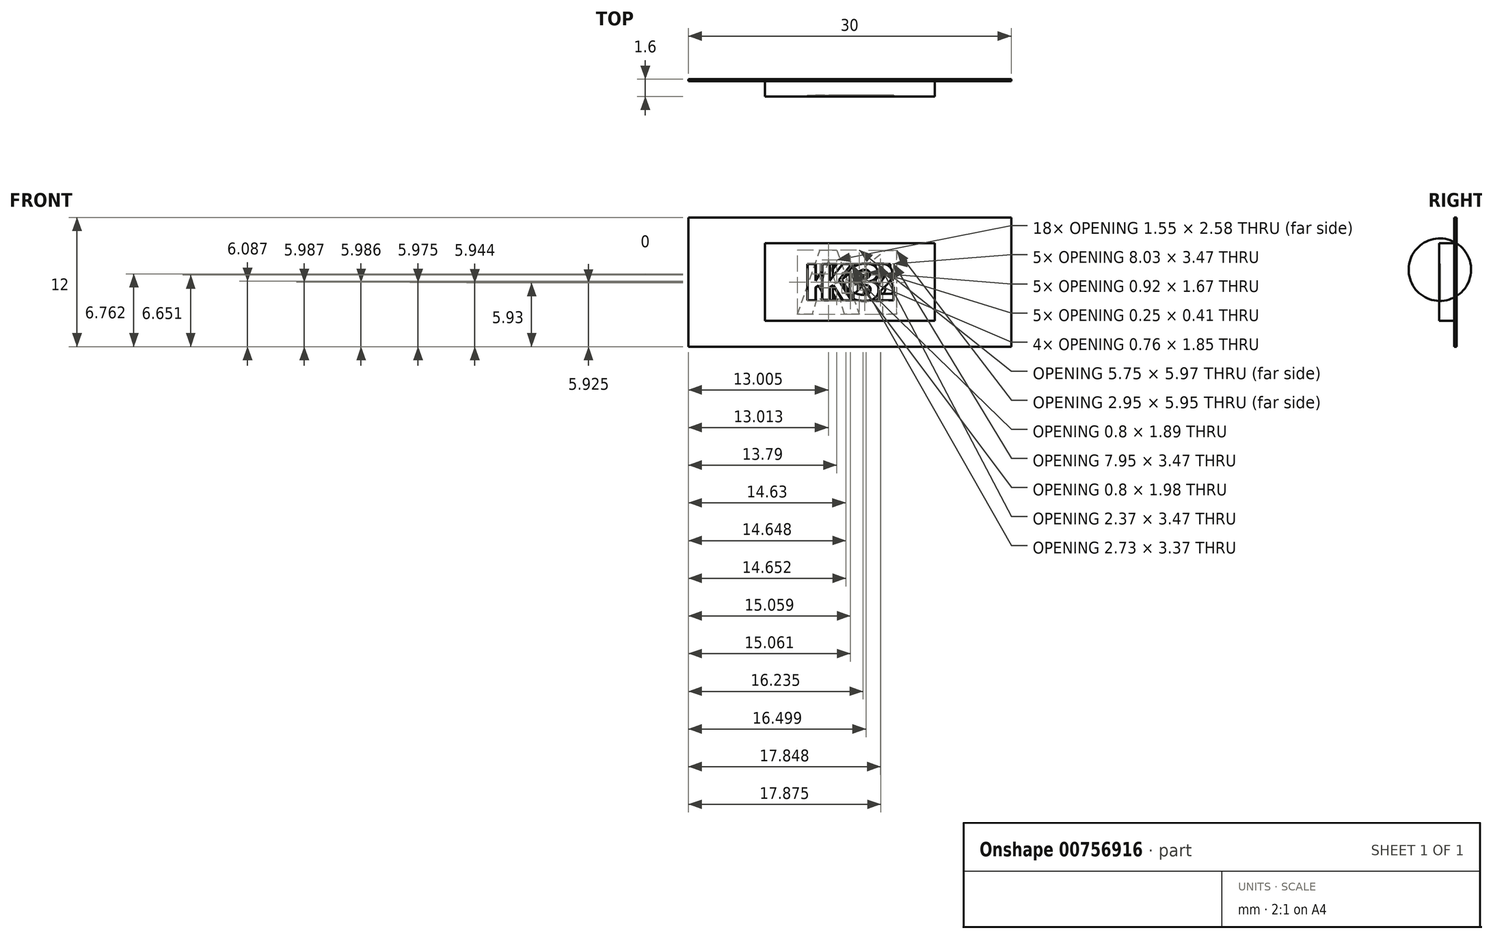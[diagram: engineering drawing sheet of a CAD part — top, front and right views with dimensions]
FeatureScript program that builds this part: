
annotation { "Feature Type Name" : "Feature", "Feature Type Description" : "" }
export const myFeature = defineFeature(function(context is Context, id is Id, definition is map)
    precondition{}
    {
        {
            var Q0;
            Q0=qCreatedBy(makeId("Front.planeOp"),FACE);
            var sketch = newSketch(context, id + "F0", { "sketchPlane" : qUnion([Q0])});
            skLineSegment(sketch, "E0.bottom", {"start": v(15, -6) * mm, "end": v(-15, -6) * mm});
            skLineSegment(sketch, "E0.top", {"start": v(15, 6) * mm, "end": v(-15, 6) * mm});
            skLineSegment(sketch, "E0.left", {"start": v(15, -6) * mm, "end": v(15, 6) * mm});
            skLineSegment(sketch, "E0.right", {"start": v(-15, -6) * mm, "end": v(-15, 6) * mm});
            skPoint(sketch, "E0.middle", {"position": v(0, 0) * mm});
            skSolve(sketch);
        }
        {
            var Q0;
            Q0 = qSketchRegion(id + "F0", true);
            extrude(context, id + "F1", {"entities" : qUnion([Q0]), "depth" : 0.2 * mm, "offsetDistance" : 25 * mm});
        }
        {
            var Q0;
            Q0=makeQuery(id+"F1.opExtrude","CAP_FACE",FACE,{"disambiguationData":[OSD([sQuery(id+"F0.wireOp",EDGE,"E0.bottom"),sQuery(id+"F0.wireOp",EDGE,"E0.top"),sQuery(id+"F0.wireOp",EDGE,"E0.left"),sQuery(id+"F0.wireOp",EDGE,"E0.right")])],"isStart":false});
            var sketch = newSketch(context, id + "F2", { "sketchPlane" : qUnion([Q0])});
            skLineSegment(sketch, "E1.bottom", {"start": v(4.87, -3) * mm, "end": v(-4.87, -3) * mm, "construction": true});
            skLineSegment(sketch, "E1.top", {"start": v(4.87, 3) * mm, "end": v(-4.87, 3) * mm, "construction": true});
            skLineSegment(sketch, "E1.left", {"start": v(4.87, -3) * mm, "end": v(4.87, 3) * mm, "construction": true});
            skLineSegment(sketch, "E1.right", {"start": v(-4.87, -3) * mm, "end": v(-4.87, 3) * mm, "construction": true});
            skPoint(sketch, "E1.middle", {"position": v(0, 0) * mm});
            skText(sketch, "E2", { "text": "A1", "fontName": "OpenSans-Bold.ttf"});
            const initialGuessF2  = {"E2": [-0.00487, -0.003, 1, 0, 0.006]};
            skSetInitialGuess(sketch, initialGuessF2);
            skSolve(sketch);
        }
        {
            var Q0;
            Q0 = qSketchRegion(id + "F2", true);
            extrude(context, id + "F3", {"entities" : qUnion([Q0]), "operationType" : NewBodyOperationType.REMOVE, "oppositeDirection" : true, "depth" : 0.1 * mm, "offsetDistance" : 25 * mm});
        }
        {
            var Q0;
            Q0=makeQuery(id+"F3.boolean.opBoolean","COPY",FACE,{"derivedFrom":makeQuery(id+"F3.opExtrude","CAP_FACE",FACE,{"disambiguationData":[OSD([sQuery(id+"F2.wireOp",EDGE,"E2.sketch_text.stroke-0"),sQuery(id+"F2.wireOp",EDGE,"E2.sketch_text.stroke-1"),sQuery(id+"F2.wireOp",EDGE,"E2.sketch_text.stroke-2"),sQuery(id+"F2.wireOp",EDGE,"E2.sketch_text.stroke-3"),sQuery(id+"F2.wireOp",EDGE,"E2.sketch_text.stroke-4"),sQuery(id+"F2.wireOp",EDGE,"E2.sketch_text.stroke-5"),sQuery(id+"F2.wireOp",EDGE,"E2.sketch_text.stroke-6"),sQuery(id+"F2.wireOp",EDGE,"E2.sketch_text.stroke-7"),sQuery(id+"F2.wireOp",EDGE,"E2.sketch_text.stroke-8"),sQuery(id+"F2.wireOp",EDGE,"E2.sketch_text.stroke-9"),sQuery(id+"F2.wireOp",EDGE,"E2.sketch_text.stroke-10"),sQuery(id+"F2.wireOp",EDGE,"E2.sketch_text.stroke-11")])],"isStart":false})});
            var Q1;
            Q1=makeQuery(id+"F3.boolean.opBoolean","COPY",FACE,{"derivedFrom":makeQuery(id+"F3.opExtrude","CAP_FACE",FACE,{"disambiguationData":[OSD([sQuery(id+"F2.wireOp",EDGE,"E2.sketch_text.stroke-12"),sQuery(id+"F2.wireOp",EDGE,"E2.sketch_text.stroke-13"),sQuery(id+"F2.wireOp",EDGE,"E2.sketch_text.stroke-14"),sQuery(id+"F2.wireOp",EDGE,"E2.sketch_text.stroke-15"),sQuery(id+"F2.wireOp",EDGE,"E2.sketch_text.stroke-16"),sQuery(id+"F2.wireOp",EDGE,"E2.sketch_text.stroke-17"),sQuery(id+"F2.wireOp",EDGE,"E2.sketch_text.stroke-18"),sQuery(id+"F2.wireOp",EDGE,"E2.sketch_text.stroke-19"),sQuery(id+"F2.wireOp",EDGE,"E2.sketch_text.stroke-20"),sQuery(id+"F2.wireOp",EDGE,"E2.sketch_text.stroke-21")])],"isStart":false})});
            var Q2;
            {var subQ0=sQuery(id+"F0.wireOp",EDGE,"E0.left");var subQ1=sQuery(id+"F0.wireOp",EDGE,"E0.bottom");var subQ2=sQuery(id+"F0.wireOp",EDGE,"E0.right");var subQ3=sQuery(id+"F0.wireOp",EDGE,"E0.top");Q2=makeQuery(id+"F3.boolean.opBoolean","SPLIT",FACE,{"disambiguationData":[TD([makeQuery(id+"F1.opExtrude","SWEPT_FACE",FACE,{"disambiguationData":[OSD([subQ1])]})])],"derivedFrom":makeQuery(id+"F1.opExtrude","CAP_FACE",FACE,{"disambiguationData":[OSD([subQ1,subQ3,subQ0,subQ2])],"isStart":false})});}
            extrude(context, id + "F4", {"entities" : qUnion([Q0, Q1]), "endBound" : BoundingType.UP_TO_SURFACE, "depth" : 25 * mm, "endBoundEntityFace" : qUnion([Q2]), "offsetDistance" : 25 * mm});
        }
        {
            var Q0;
            Q0=qCreatedBy(makeId("Front.planeOp"),FACE);
            var sketch = newSketch(context, id + "F5", { "sketchPlane" : qUnion([Q0])});
            skLineSegment(sketch, "E3.bottom", {"start": v(7.9, -3.6) * mm, "end": v(-7.9, -3.6) * mm});
            skLineSegment(sketch, "E3.top", {"start": v(7.9, 3.6) * mm, "end": v(-7.9, 3.6) * mm});
            skLineSegment(sketch, "E3.left", {"start": v(7.9, -3.6) * mm, "end": v(7.9, 3.6) * mm});
            skLineSegment(sketch, "E3.right", {"start": v(-7.9, -3.6) * mm, "end": v(-7.9, 3.6) * mm});
            skPoint(sketch, "E3.middle", {"position": v(0, 0) * mm});
            skSolve(sketch);
        }
        {
            var Q0;
            Q0 = qSketchRegion(id + "F5", true);
            extrude(context, id + "F6", {"entities" : qUnion([Q0]), "depth" : 1.6 * mm, "offsetDistance" : 25 * mm});
        }
        {
            var Q0;
            Q0=makeQuery(id+"F6.opExtrude","CAP_FACE",FACE,{"disambiguationData":[OSD([sQuery(id+"F5.wireOp",EDGE,"E3.bottom"),sQuery(id+"F5.wireOp",EDGE,"E3.top"),sQuery(id+"F5.wireOp",EDGE,"E3.left"),sQuery(id+"F5.wireOp",EDGE,"E3.right")])],"isStart":false});
            var sketch = newSketch(context, id + "F7", { "sketchPlane" : qUnion([Q0])});
            skLineSegment(sketch, "E4.bottom", {"start": v(4.33, -1.7) * mm, "end": v(-4.33, -1.7) * mm, "construction": true});
            skLineSegment(sketch, "E4.top", {"start": v(4.33, 1.7) * mm, "end": v(-4.33, 1.7) * mm, "construction": true});
            skLineSegment(sketch, "E4.left", {"start": v(4.33, -1.7) * mm, "end": v(4.33, 1.7) * mm, "construction": true});
            skLineSegment(sketch, "E4.right", {"start": v(-4.33, -1.7) * mm, "end": v(-4.33, 1.7) * mm, "construction": true});
            skPoint(sketch, "E4.middle", {"position": v(0, 0) * mm});
            skText(sketch, "E5", { "text": "K13", "fontName": "OpenSans-Bold.ttf"});
            const initialGuessF7  = {"E5": [-0.00433, -0.0017, 1, 0, 0.0034]};
            skSetInitialGuess(sketch, initialGuessF7);
            skSolve(sketch);
        }
        {
            var Q0;
            Q0 = qSketchRegion(id + "F7", true);
            extrude(context, id + "F8", {"entities" : qUnion([Q0]), "operationType" : NewBodyOperationType.REMOVE, "oppositeDirection" : true, "depth" : 0.1 * mm, "offsetDistance" : 25 * mm});
        }
        {
            var Q0;
            Q0 = qSketchRegion(id + "F5", true);
            extrude(context, id + "F9", {"entities" : qUnion([Q0]), "depth" : 1.6 * mm, "offsetDistance" : 25 * mm});
        }
        {
            var Q0;
            Q0=makeQuery(id+"F9.opExtrude","CAP_FACE",FACE,{"disambiguationData":[OSD([sQuery(id+"F5.wireOp",EDGE,"E3.bottom"),sQuery(id+"F5.wireOp",EDGE,"E3.top"),sQuery(id+"F5.wireOp",EDGE,"E3.left"),sQuery(id+"F5.wireOp",EDGE,"E3.right")])],"isStart":false});
            var sketch = newSketch(context, id + "F10", { "sketchPlane" : qUnion([Q0])});
            skLineSegment(sketch, "E6.bottom", {"start": v(4.38, -1.7) * mm, "end": v(-4.38, -1.7) * mm, "construction": true});
            skLineSegment(sketch, "E6.top", {"start": v(4.38, 1.7) * mm, "end": v(-4.38, 1.7) * mm, "construction": true});
            skLineSegment(sketch, "E6.left", {"start": v(4.38, -1.7) * mm, "end": v(4.38, 1.7) * mm, "construction": true});
            skLineSegment(sketch, "E6.right", {"start": v(-4.38, -1.7) * mm, "end": v(-4.38, 1.7) * mm, "construction": true});
            skPoint(sketch, "E6.middle", {"position": v(0, 0) * mm});
            skText(sketch, "E7", { "text": "K14", "fontName": "OpenSans-Bold.ttf"});
            const initialGuessF10  = {"E7": [-0.00438, -0.0017, 1, 0, 0.0034]};
            skSetInitialGuess(sketch, initialGuessF10);
            skSolve(sketch);
        }
        {
            var Q0;
            Q0 = qSketchRegion(id + "F10", true);
            extrude(context, id + "F11", {"entities" : qUnion([Q0]), "operationType" : NewBodyOperationType.REMOVE, "oppositeDirection" : true, "depth" : 0.1 * mm, "offsetDistance" : 25 * mm});
        }
        {
            var Q0;
            Q0 = qSketchRegion(id + "F5", true);
            extrude(context, id + "F12", {"entities" : qUnion([Q0]), "depth" : 1.6 * mm, "offsetDistance" : 25 * mm});
        }
        {
            var Q0;
            Q0=makeQuery(id+"F12.opExtrude","CAP_FACE",FACE,{"disambiguationData":[OSD([sQuery(id+"F5.wireOp",EDGE,"E3.bottom"),sQuery(id+"F5.wireOp",EDGE,"E3.top"),sQuery(id+"F5.wireOp",EDGE,"E3.left"),sQuery(id+"F5.wireOp",EDGE,"E3.right")])],"isStart":false});
            var sketch = newSketch(context, id + "F13", { "sketchPlane" : qUnion([Q0])});
            skLineSegment(sketch, "E8.bottom", {"start": v(4.31, -1.7) * mm, "end": v(-4.31, -1.7) * mm, "construction": true});
            skLineSegment(sketch, "E8.top", {"start": v(4.31, 1.7) * mm, "end": v(-4.31, 1.7) * mm, "construction": true});
            skLineSegment(sketch, "E8.left", {"start": v(4.31, -1.7) * mm, "end": v(4.31, 1.7) * mm, "construction": true});
            skLineSegment(sketch, "E8.right", {"start": v(-4.31, -1.7) * mm, "end": v(-4.31, 1.7) * mm, "construction": true});
            skPoint(sketch, "E8.middle", {"position": v(0, 0) * mm});
            skText(sketch, "E9", { "text": "K15", "fontName": "OpenSans-Bold.ttf"});
            const initialGuessF13  = {"E9": [-0.00431, -0.0017, 1, 0, 0.0034]};
            skSetInitialGuess(sketch, initialGuessF13);
            skSolve(sketch);
        }
        {
            var Q0;
            Q0 = qSketchRegion(id + "F13", true);
            extrude(context, id + "F14", {"entities" : qUnion([Q0]), "operationType" : NewBodyOperationType.REMOVE, "oppositeDirection" : true, "depth" : 0.1 * mm, "offsetDistance" : 25 * mm});
        }
        {
            var Q0;
            Q0 = qSketchRegion(id + "F5", true);
            extrude(context, id + "F15", {"entities" : qUnion([Q0]), "depth" : 1.6 * mm, "offsetDistance" : 25 * mm});
        }
        {
            var Q0;
            Q0=makeQuery(id+"F15.opExtrude","CAP_FACE",FACE,{"disambiguationData":[OSD([sQuery(id+"F5.wireOp",EDGE,"E3.bottom"),sQuery(id+"F5.wireOp",EDGE,"E3.top"),sQuery(id+"F5.wireOp",EDGE,"E3.left"),sQuery(id+"F5.wireOp",EDGE,"E3.right")])],"isStart":false});
            var sketch = newSketch(context, id + "F16", { "sketchPlane" : qUnion([Q0])});
            skLineSegment(sketch, "E10.bottom", {"start": v(4.34, -1.7) * mm, "end": v(-4.34, -1.7) * mm, "construction": true});
            skLineSegment(sketch, "E10.top", {"start": v(4.34, 1.7) * mm, "end": v(-4.34, 1.7) * mm, "construction": true});
            skLineSegment(sketch, "E10.left", {"start": v(4.34, -1.7) * mm, "end": v(4.34, 1.7) * mm, "construction": true});
            skLineSegment(sketch, "E10.right", {"start": v(-4.34, -1.7) * mm, "end": v(-4.34, 1.7) * mm, "construction": true});
            skPoint(sketch, "E10.middle", {"position": v(0, 0) * mm});
            skText(sketch, "E11", { "text": "K12", "fontName": "OpenSans-Bold.ttf"});
            const initialGuessF16  = {"E11": [-0.00434, -0.0017, 1, 0, 0.0034]};
            skSetInitialGuess(sketch, initialGuessF16);
            skSolve(sketch);
        }
        {
            var Q0;
            Q0 = qSketchRegion(id + "F16", true);
            extrude(context, id + "F17", {"entities" : qUnion([Q0]), "operationType" : NewBodyOperationType.REMOVE, "oppositeDirection" : true, "depth" : 0.1 * mm, "offsetDistance" : 25 * mm});
        }
        {
            var Q0;
            Q0 = qSketchRegion(id + "F5", true);
            extrude(context, id + "F18", {"entities" : qUnion([Q0]), "depth" : 1.6 * mm, "offsetDistance" : 25 * mm});
        }
        {
            var Q0;
            Q0=makeQuery(id+"F18.opExtrude","CAP_FACE",FACE,{"disambiguationData":[OSD([sQuery(id+"F5.wireOp",EDGE,"E3.bottom"),sQuery(id+"F5.wireOp",EDGE,"E3.top"),sQuery(id+"F5.wireOp",EDGE,"E3.left"),sQuery(id+"F5.wireOp",EDGE,"E3.right")])],"isStart":false});
            var sketch = newSketch(context, id + "F19", { "sketchPlane" : qUnion([Q0])});
            skLineSegment(sketch, "E12.bottom", {"start": v(2.7, -1.7) * mm, "end": v(-2.7, -1.7) * mm, "construction": true});
            skLineSegment(sketch, "E12.top", {"start": v(2.7, 1.7) * mm, "end": v(-2.7, 1.7) * mm, "construction": true});
            skLineSegment(sketch, "E12.left", {"start": v(2.7, -1.7) * mm, "end": v(2.7, 1.7) * mm, "construction": true});
            skLineSegment(sketch, "E12.right", {"start": v(-2.7, -1.7) * mm, "end": v(-2.7, 1.7) * mm, "construction": true});
            skPoint(sketch, "E12.middle", {"position": v(0, 0) * mm});
            skText(sketch, "E13", { "text": "K1", "fontName": "OpenSans-Bold.ttf"});
            const initialGuessF19  = {"E13": [-0.0027, -0.0017, 1, 0, 0.0034]};
            skSetInitialGuess(sketch, initialGuessF19);
            skSolve(sketch);
        }
        {
            var Q0;
            Q0 = qSketchRegion(id + "F19", true);
            extrude(context, id + "F20", {"entities" : qUnion([Q0]), "operationType" : NewBodyOperationType.REMOVE, "oppositeDirection" : true, "depth" : 0.1 * mm, "offsetDistance" : 25 * mm});
        }
        {
            var Q0;
            Q0 = qSketchRegion(id + "F5", true);
            extrude(context, id + "F21", {"entities" : qUnion([Q0]), "depth" : 1.6 * mm, "offsetDistance" : 25 * mm});
        }
        {
            var Q0;
            Q0=makeQuery(id+"F21.opExtrude","CAP_FACE",FACE,{"disambiguationData":[OSD([sQuery(id+"F5.wireOp",EDGE,"E3.bottom"),sQuery(id+"F5.wireOp",EDGE,"E3.top"),sQuery(id+"F5.wireOp",EDGE,"E3.left"),sQuery(id+"F5.wireOp",EDGE,"E3.right")])],"isStart":false});
            var sketch = newSketch(context, id + "F22", { "sketchPlane" : qUnion([Q0])});
            skLineSegment(sketch, "E14.bottom", {"start": v(3, -1.7) * mm, "end": v(-3, -1.7) * mm, "construction": true});
            skLineSegment(sketch, "E14.top", {"start": v(3, 1.7) * mm, "end": v(-3, 1.7) * mm, "construction": true});
            skLineSegment(sketch, "E14.left", {"start": v(3, -1.7) * mm, "end": v(3, 1.7) * mm, "construction": true});
            skLineSegment(sketch, "E14.right", {"start": v(-3, -1.7) * mm, "end": v(-3, 1.7) * mm, "construction": true});
            skPoint(sketch, "E14.middle", {"position": v(0, 0) * mm});
            skText(sketch, "E15", { "text": "K2", "fontName": "OpenSans-Bold.ttf"});
            const initialGuessF22  = {"E15": [-0.003, -0.0017, 1, 0, 0.0034]};
            skSetInitialGuess(sketch, initialGuessF22);
            skSolve(sketch);
        }
        {
            var Q0;
            Q0 = qSketchRegion(id + "F22", true);
            extrude(context, id + "F23", {"entities" : qUnion([Q0]), "operationType" : NewBodyOperationType.REMOVE, "oppositeDirection" : true, "depth" : 0.1 * mm, "offsetDistance" : 25 * mm});
        }
        {
            var Q0;
            Q0 = qSketchRegion(id + "F5", true);
            extrude(context, id + "F24", {"entities" : qUnion([Q0]), "depth" : 1.6 * mm, "offsetDistance" : 25 * mm});
        }
        {
            var Q0;
            Q0=makeQuery(id+"F24.opExtrude","CAP_FACE",FACE,{"disambiguationData":[OSD([sQuery(id+"F5.wireOp",EDGE,"E3.bottom"),sQuery(id+"F5.wireOp",EDGE,"E3.top"),sQuery(id+"F5.wireOp",EDGE,"E3.left"),sQuery(id+"F5.wireOp",EDGE,"E3.right")])],"isStart":false});
            var sketch = newSketch(context, id + "F25", { "sketchPlane" : qUnion([Q0])});
            skLineSegment(sketch, "E16.bottom", {"start": v(2.98, -1.7) * mm, "end": v(-2.98, -1.7) * mm, "construction": true});
            skLineSegment(sketch, "E16.top", {"start": v(2.98, 1.7) * mm, "end": v(-2.98, 1.7) * mm, "construction": true});
            skLineSegment(sketch, "E16.left", {"start": v(2.98, -1.7) * mm, "end": v(2.98, 1.7) * mm, "construction": true});
            skLineSegment(sketch, "E16.right", {"start": v(-2.98, -1.7) * mm, "end": v(-2.98, 1.7) * mm, "construction": true});
            skPoint(sketch, "E16.middle", {"position": v(0, 0) * mm});
            skText(sketch, "E17", { "text": "K3", "fontName": "OpenSans-Bold.ttf"});
            const initialGuessF25  = {"E17": [-0.00298, -0.0017, 1, 0, 0.0034]};
            skSetInitialGuess(sketch, initialGuessF25);
            skSolve(sketch);
        }
        {
            var Q0;
            Q0 = qSketchRegion(id + "F25", true);
            extrude(context, id + "F26", {"entities" : qUnion([Q0]), "operationType" : NewBodyOperationType.REMOVE, "oppositeDirection" : true, "depth" : 0.1 * mm, "offsetDistance" : 25 * mm});
        }
        {
            var Q0;
            Q0 = qSketchRegion(id + "F5", true);
            extrude(context, id + "F27", {"entities" : qUnion([Q0]), "depth" : 1.6 * mm, "offsetDistance" : 25 * mm});
        }
    });
